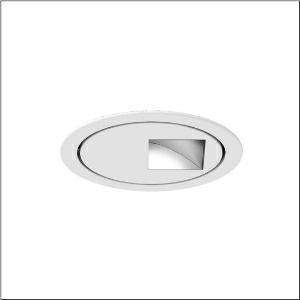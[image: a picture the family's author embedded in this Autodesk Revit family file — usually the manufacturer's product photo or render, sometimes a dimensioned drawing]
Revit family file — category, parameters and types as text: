
# Revit family: lunis_11_mini_round_51dk11b72wm21
name_source: partatom
category: Lighting Fixtures
units: mm (PartAtom-declared; Revit-internal decimal feet)

## family parameters
Cut with Voids When Loaded = No
Host = Face
Light Source = No
Part Type = Normal
Room Calculation Point = No
Round Connector Dimension = Use Diameter
Shared = No

## types (1)
- Lunis 11 mini round (1 x LED 3000K / CRI = 90 (unbekannt), 1930 lm, 3000K)
    Apparent Load = 28 VA
    CIE Flux Codes = 44 77 97 100 100
    Color Rendering = 90
    Color Temperature = 3000K
    Default Elevation = 1800 mm
    Description = Lunis 11 mini round, downlight, light control with wallwasher, of highly reflective aluminium, highly specular, light emission: direct distribution, LED rated luminous flux: 1.930lm, light colour: 930, control gear: ECG, with terminal, 3-pole, mains connection: 220..230V, AC/DC, 0/50..60Hz, LED module, luminaire module, of aluminium, highly specular, white, diameter: 176mm, clamping range: 1..40mm, recessing ring, of plastic, traffic white (RAL 9016), protection rating (complete): IP20, insulation class (complete): insulation class II (safety insulation), certification: CE, permissible ambient temperature for indoor applications: 0..+35°C, packaging unit: 1 piece
    Height = 0 mm  [stored 0 ft]
    Lamp = 1 x LED 3000K / CRI >= 90 (unbekannt)
    Lamp Light Flux = 1930 lm
    Lamp count = 1
    Length = 176 mm
    Luminous efficacy = 69 lm/W
    Manufacturer = Siteco
    ModVariant = No
    Model = 51DK11B72WM21
    Mounting Place = Ceiling
    Mounting Type = Recessed
    Number of Poles = 1
    OnlyDefault = Yes
    Power Factor = 1
    Product Name = Lunis 11 mini round
    Product group = downlight
    ProductGroupID = 401
    Protection Class = Protection class II
    Protection Degree = IP 20
    RLX_Detail_Level = 1
    RLX_Emergency_Light_Flux = 0 lm
    RLX_Emergency_Type = 0
    RLX_Emergency_Type_DB = No
    RlxData = <blob elided: 59233 chars, md5=d420615e>
    Socket = socket
    Standby Power = 0 W
    System Light Flux = 1930 lm
    System Power = 28 W
    Type Comments = Product without accessories
    Type Image = l_1004772.jpg
    URL = http://relux.com
    VarID = ---
    Voltage = 0 V
    Weight = 0.00 kg
    Width = 176 mm

note: [stored X ft] marks values corroborated as IEEE doubles in the binary element streams (Revit-internal decimal feet)

## geometry (parser evidence)
native form markers: Blend x4, Sweep x12
no freeform markers — native parametric forms only
